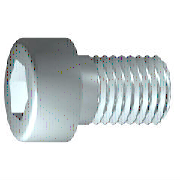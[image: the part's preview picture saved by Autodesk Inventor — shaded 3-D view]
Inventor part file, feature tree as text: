
AUTODESK INVENTOR PART (.ipt)
format: ipt  version: 2022 (Build 260153000, 153)  size: 191,488 bytes
history: native  units: mm (DEFAULTED — no unit token found)
features: sketch x2, extrude x1, plane x1
ambient origin geometry x7: Origin, YZ Plane, XY Plane, X Axis, Y Axis, Z Axis, Center Point
bodies: Solid1 (feature_tree), Body (feature_tree)
feature tree (4):
  extrude  "Slot"  Depth=0.306725mm
  plane  "Work Plane1"
  sketch  "Sketch1"  dims[d0=8.693275mm d1=0.306725mm]
  sketch  "Sketch2"  dims[d2=3.0mm d3=1.5mm d4=60.0deg d5=3.0mm d6=3.0mm d7=2.886751mm d8=5.5mm d10=90.0deg d11=10.0mm d9=0.0mm d12=8.693275mm d13=0.0mm d14=0.306725mm d15=0.306725mm d16=0.3mm d17=0.0mm d18=0.0mm d19=10.0mm d27=45.0deg d28=0.1mm d29=0.1mm]
